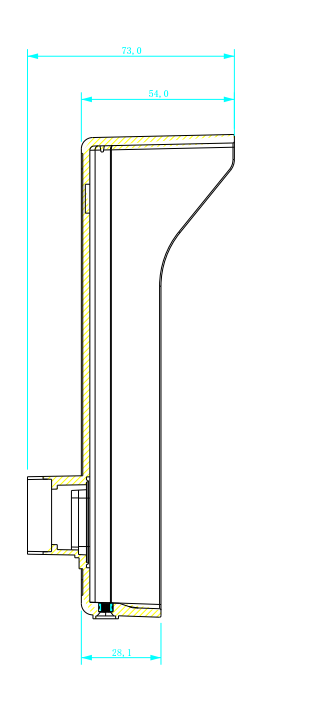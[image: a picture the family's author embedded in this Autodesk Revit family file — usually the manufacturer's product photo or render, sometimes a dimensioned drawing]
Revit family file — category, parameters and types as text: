
# Revit family: AM-02
name_source: partatom
category: Устройства связи
units: mm (PartAtom-declared; Revit-internal decimal feet)

## family parameters
Всегда вертикально = Нет
На основе рабочей плоскости = Да
Общий = Да
При загрузке вырезать с полостями = Нет
Размер круглого соединителя = Использовать диаметр
Сохранять ориентацию аннотаций = Нет
Тип детали = Нормальный
Точка принадлежности помещению = Нет

## types (1)
- AM-02
    ADSK_URL документации изделия = https://wiki.bas-ip.com
    ADSK_URL страницы изделия = https://www.bas-ip.ru
    ADSK_Версия Revit = Revit 2020
    ADSK_Единица измерения = шт
    ADSK_Завод-изготовитель = BAS-IP
    ADSK_Классификация нагрузок = Монитор консьержа
    ADSK_Количество фаз = 1
    ADSK_Коэффициент мощности = 0.9
    ADSK_Марка = AM-02
    ADSK_Наименование = Монитор консьержа AM-02
    ADSK_Наименование краткое = AM-02
    ADSK_Напряжение = 12 В
    ADSK_Размер_Длина = 194 мм
    ADSK_Размер_Толщина = 64 мм
    ADSK_Размер_Ширина = 303 мм
    BIM library = https://bimlib.ru
    URL = https://www.bas-ip.ru
    Группа модели = Монитор консьержа
    Дисплей = 10.1” TFT LCD, сенсорный
    Дополнительно = 6 уровней громкости; Режим "Без звука"; Режим "Не беспокоить"; Поддержка протокола SIP 2.0
    Допустимая влажность воздуха = 20-80%
    Изготовитель = BAS-IP
    Изображение типоразмера = <Нет>
    Интернет протокол = IPv4
    Интерфейс = WEB–интерфейс, GUI
    Количество кнопок управления = 2
    Материал корпуса = Материал серый
    Описание = Основные преимущества монитора консьержа AM-02:
• Записная книга;
• Установка сторонних приложений;
• Выбор типа заставки в режиме ожидания ("Тур", "Квадратор");
• Гибкая настройка вида главного экрана пользователем;
• Простая система поиска контактов и возможность подключится к любому устройству BAS-IP;
• Добавление собственных рингтонов;
• Получение обновлений прошивок напрямую с сервера.
    Отметка по умолчанию = 0 мм
    Питание = + 12 В, PoE
    Поддерживаемые кодеки = G.711u, H.264
    Поддержка IP камер = До 100 штук
    Поддержка VoIP аккаунтов = 1
    Подключение к сети = Ethernet10/Base100-T, 8P8C
    Размеры = 303х194х64 мм
    Температурный режим = -10 ... +55 °С
    Тип установки = Настольная установка
    Управление замком = Да
